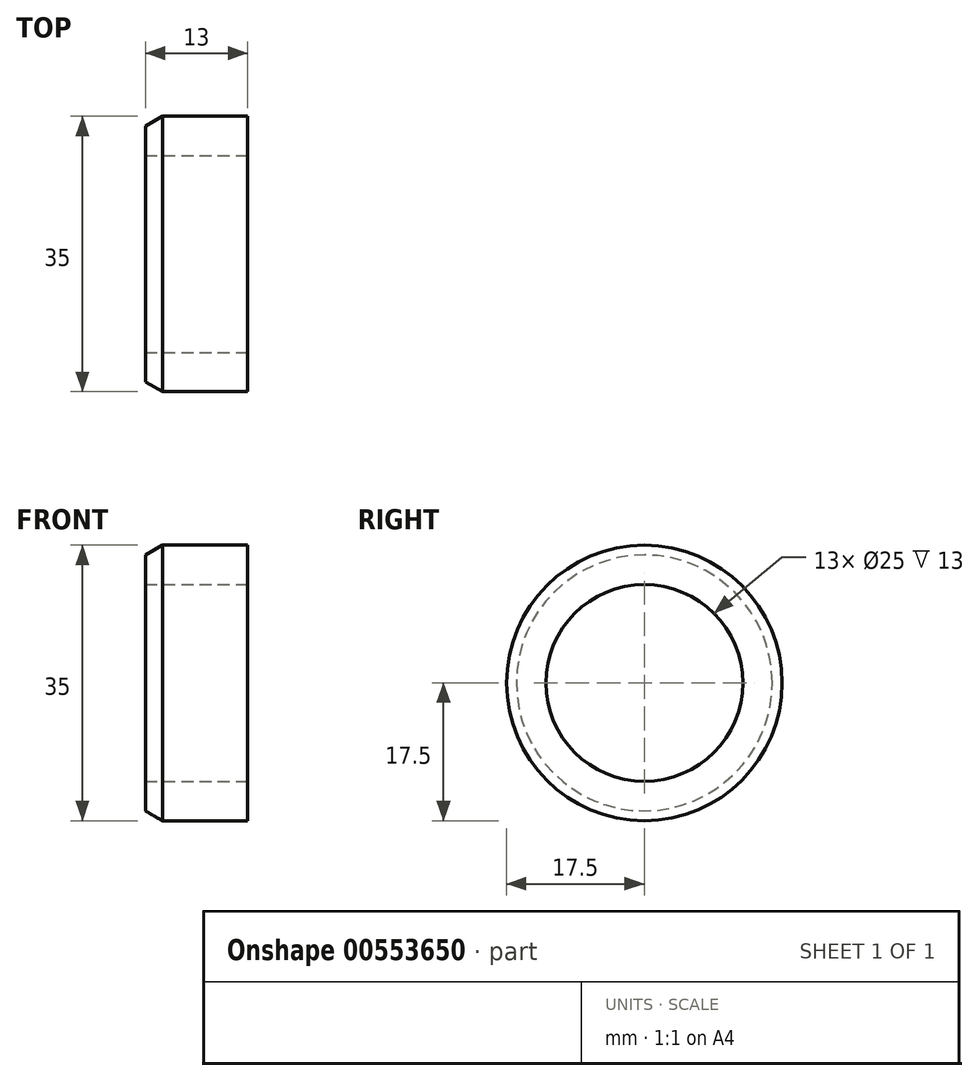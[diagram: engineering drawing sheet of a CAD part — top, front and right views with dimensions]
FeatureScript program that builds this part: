
annotation { "Feature Type Name" : "Feature", "Feature Type Description" : "" }
export const myFeature = defineFeature(function(context is Context, id is Id, definition is map)
    precondition{}
    {
        {
            var Q0;
            Q0=qCreatedBy(makeId("Front.planeOp"),FACE);
            var sketch = newSketch(context, id + "F0", { "sketchPlane" : qUnion([Q0])});
            skLineSegment(sketch, "E0", {"start": v(0, 17.5) * mm, "end": v(-10.83, 17.5) * mm});
            skLineSegment(sketch, "E1", {"start": v(-10.83, 17.5) * mm, "end": v(-13, 16.25) * mm});
            skLineSegment(sketch, "E2", {"start": v(-13, 16.25) * mm, "end": v(-13, 12.5) * mm});
            skLineSegment(sketch, "E3", {"start": v(-13, 12.5) * mm, "end": v(0, 12.5) * mm});
            skLineSegment(sketch, "E4", {"start": v(0, 12.5) * mm, "end": v(0, 17.5) * mm});
            skLineSegment(sketch, "E5", {"start": v(0, 0) * mm, "end": v(-13, 0) * mm, "construction": true});
            skSolve(sketch);
        }
        {
            var Q0;
            Q0 = qSketchRegion(id + "F0", true);
            var Q1;
            Q1=sQuery(id+"F0.wireOp",EDGE,"E5");
            revolve(context, id + "F1", {"entities" : qUnion([Q0]), "axis" : qUnion([Q1]), "revolveType" : RevolveType.FULL});
        }
    });
